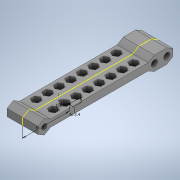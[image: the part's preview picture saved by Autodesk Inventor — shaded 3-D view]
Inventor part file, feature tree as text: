
AUTODESK INVENTOR PART (.ipt)
format: ipt  version: 2020 (Build 240168000, 168)  size: 446,976 bytes
history: native  units: in
note: dims shown in document units (in); Inventor stores cm internally (conversion verified against a paired STEP export)
features: sketch x7, extrude x5, projected_geometry x4, plane x2, mirror x1
ambient origin geometry x8: Origin, YZ Plane, XZ Plane, XY Plane, X Axis, Y Axis, Z Axis, Center Point
bodies: Solid1 (feature_tree)
feature tree (19):
  extrude  "Extrusion1"  Depth=3.4256in
  plane  "Work Plane1"
  extrude  "Extrusion2"  Depth=0.7874in
  sketch  "Sketch4"  dims[d4=0.0in d5=0.0827in]
  extrude  "Extrusion4"  Depth=0.0827in
  plane  "Work Plane2"
  extrude  "Extrusion6"  Depth=3.1106in
  mirror  "Mirror2"
  extrude  "Extrusion7"  Depth=0.315in
  sketch  "Sketch10"  dims[d34=0.2362in d35=0.0in d38=0.315in d39=0.2756in d40=-0.3092in d41=0.0787in d42=0.0787in d43=0.0787in d44=3.1496in d46=0.2913in d47=0.3937in d49=0.3937in d51=3.1496in d53=0.2913in d54=0.3937in d56=0.3937in d58=0.0in d59=0.0in d60=150.0deg d61=0.1339in d62=0.1181in d63=1.1811in]
  sketch  "Sketch1"  dims[d0=0.1818in d1=3.4256in]
  sketch  "Sketch2"  dims[d2=0.1339in d3=0.7874in]
  sketch  "Sketch5"  dims[d6=0.7874in d7=0.0in d28=3.1106in]
  sketch  "Sketch7"  dims[d29=0.315in d31=0.315in]
  projected_geometry  "Projected Loop7"
  projected_geometry  "Projected Loop8"
  sketch  "Sketch8"  dims[d33=0.1575in]
  projected_geometry  "Projected Loop9"
  projected_geometry  "Projected Loop10"
